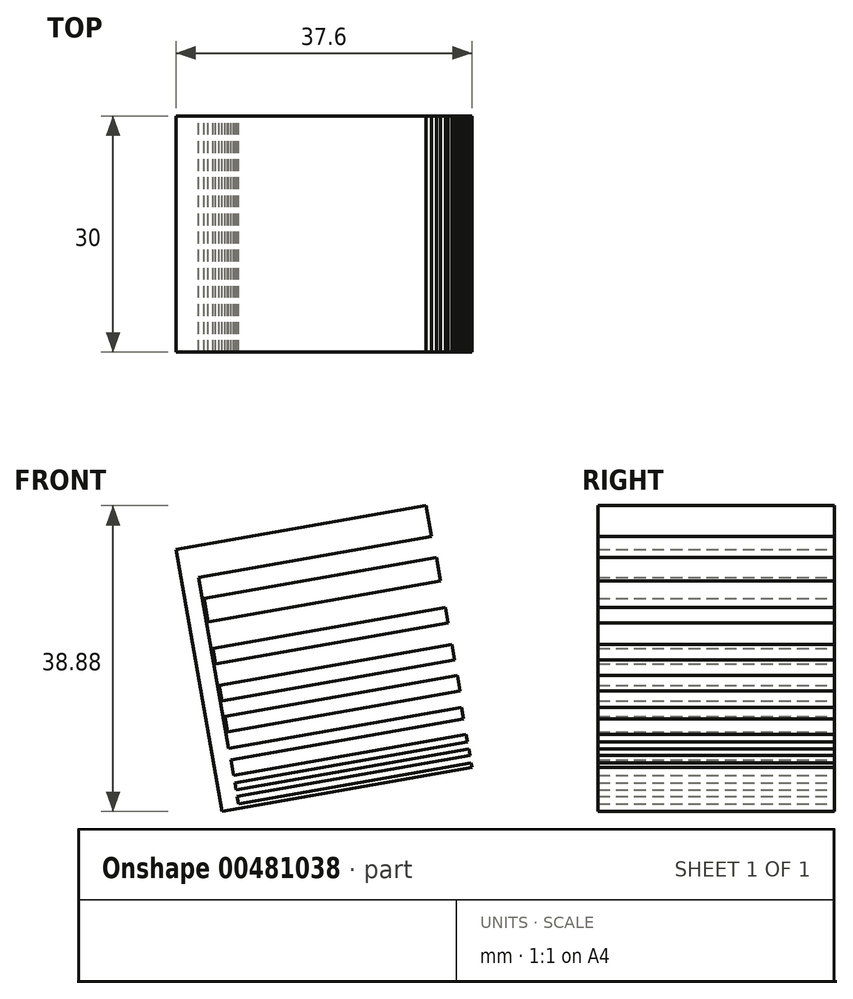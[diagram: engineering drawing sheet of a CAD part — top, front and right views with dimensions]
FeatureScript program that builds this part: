
annotation { "Feature Type Name" : "Feature", "Feature Type Description" : "" }
export const myFeature = defineFeature(function(context is Context, id is Id, definition is map)
    precondition{}
    {
        {
            var Q0;
            Q0=qCreatedBy(makeId("Front.planeOp"),FACE);
            var sketch = newSketch(context, id + "F0", { "sketchPlane" : qUnion([Q0])});
            skLineSegment(sketch, "E0.bottom", {"start": v(37.84, 14.06) * mm, "end": v(39.84, 14.06) * mm});
            skLineSegment(sketch, "E0.top", {"start": v(37.84, -15.94) * mm, "end": v(39.84, -15.94) * mm});
            skLineSegment(sketch, "E0.left", {"start": v(37.84, 14.06) * mm, "end": v(37.84, -15.94) * mm});
            skLineSegment(sketch, "E0.right", {"start": v(39.84, 14.06) * mm, "end": v(39.84, -15.94) * mm});
            skLineSegment(sketch, "E1.bottom", {"start": v(33.84, 14.06) * mm, "end": v(35.84, 14.06) * mm});
            skLineSegment(sketch, "E1.top", {"start": v(33.84, -15.94) * mm, "end": v(35.84, -15.94) * mm});
            skLineSegment(sketch, "E1.left", {"start": v(33.84, 14.06) * mm, "end": v(33.84, -15.94) * mm});
            skLineSegment(sketch, "E1.right", {"start": v(35.84, 14.06) * mm, "end": v(35.84, -15.94) * mm});
            skLineSegment(sketch, "E2.bottom", {"start": v(29.09, 14.06) * mm, "end": v(31.09, 14.06) * mm});
            skLineSegment(sketch, "E2.top", {"start": v(29.09, -15.94) * mm, "end": v(31.09, -15.94) * mm});
            skLineSegment(sketch, "E2.left", {"start": v(29.09, 14.06) * mm, "end": v(29.09, -15.94) * mm});
            skLineSegment(sketch, "E2.right", {"start": v(31.09, 14.06) * mm, "end": v(31.09, -15.94) * mm});
            skLineSegment(sketch, "E3.bottom", {"start": v(22.64, 14.06) * mm, "end": v(25.64, 14.06) * mm});
            skLineSegment(sketch, "E3.top", {"start": v(22.64, -15.94) * mm, "end": v(25.64, -15.94) * mm});
            skLineSegment(sketch, "E3.left", {"start": v(22.64, 14.06) * mm, "end": v(22.64, -15.94) * mm});
            skLineSegment(sketch, "E3.right", {"start": v(25.64, 14.06) * mm, "end": v(25.64, -15.94) * mm});
            skLineSegment(sketch, "E4.bottom", {"start": v(15.9, 13.86) * mm, "end": v(19.9, 13.86) * mm});
            skLineSegment(sketch, "E4.top", {"start": v(15.9, -16.14) * mm, "end": v(19.9, -16.14) * mm});
            skLineSegment(sketch, "E4.left", {"start": v(15.9, 13.86) * mm, "end": v(15.9, -16.14) * mm});
            skLineSegment(sketch, "E4.right", {"start": v(19.9, 13.86) * mm, "end": v(19.9, -16.14) * mm});
            skLineSegment(sketch, "E5.bottom", {"start": v(41.93, 13.86) * mm, "end": v(43.43, 13.86) * mm});
            skLineSegment(sketch, "E5.top", {"start": v(41.93, -16.14) * mm, "end": v(43.43, -16.14) * mm});
            skLineSegment(sketch, "E5.left", {"start": v(41.93, 13.86) * mm, "end": v(41.93, -16.14) * mm});
            skLineSegment(sketch, "E5.right", {"start": v(43.43, 13.86) * mm, "end": v(43.43, -16.14) * mm});
            skLineSegment(sketch, "E6.bottom", {"start": v(49.1, 13.86) * mm, "end": v(49.7, 13.86) * mm});
            skLineSegment(sketch, "E6.top", {"start": v(49.1, -16.14) * mm, "end": v(49.7, -16.14) * mm});
            skLineSegment(sketch, "E6.left", {"start": v(49.1, 13.86) * mm, "end": v(49.1, -16.14) * mm});
            skLineSegment(sketch, "E6.right", {"start": v(49.7, 13.86) * mm, "end": v(49.7, -16.14) * mm});
            skLineSegment(sketch, "E7.bottom", {"start": v(15.9, -16.14) * mm, "end": v(49.7, -16.14) * mm});
            skLineSegment(sketch, "E7.top", {"start": v(15.9, -18.36) * mm, "end": v(49.7, -18.36) * mm});
            skLineSegment(sketch, "E7.left", {"start": v(15.9, -16.14) * mm, "end": v(15.9, -18.36) * mm});
            skLineSegment(sketch, "E7.right", {"start": v(49.7, -16.14) * mm, "end": v(49.7, -18.36) * mm});
            skLineSegment(sketch, "E8.bottom", {"start": v(45.4, 13.86) * mm, "end": v(46.4, 13.86) * mm});
            skLineSegment(sketch, "E8.top", {"start": v(45.4, -16.14) * mm, "end": v(46.4, -16.14) * mm});
            skLineSegment(sketch, "E8.left", {"start": v(45.4, 13.86) * mm, "end": v(45.4, -16.14) * mm});
            skLineSegment(sketch, "E8.right", {"start": v(46.4, 13.86) * mm, "end": v(46.4, -16.14) * mm});
            skLineSegment(sketch, "E9.bottom", {"start": v(47.3, 13.86) * mm, "end": v(48.1, 13.86) * mm});
            skLineSegment(sketch, "E9.top", {"start": v(47.3, -16.14) * mm, "end": v(48.1, -16.14) * mm});
            skLineSegment(sketch, "E9.left", {"start": v(47.3, 13.86) * mm, "end": v(47.3, -16.14) * mm});
            skLineSegment(sketch, "E9.right", {"start": v(48.1, 13.86) * mm, "end": v(48.1, -16.14) * mm});
            skSolve(sketch);
        }
        {
            var Q0;
            Q0=makeQuery(id+"F0.imprint","IMPRINT",FACE,{"disambiguationData":[TD([[makeQuery(id+"F0.imprint","IMPRINT",EDGE,{"derivedFrom":sQuery(id+"F0.wireOp",EDGE,"E6.bottom")}),-1.0]])]});
            var Q1;
            Q1=makeQuery(id+"F0.imprint","IMPRINT",FACE,{"disambiguationData":[TD([[makeQuery(id+"F0.imprint","IMPRINT",EDGE,{"derivedFrom":sQuery(id+"F0.wireOp",EDGE,"E5.bottom")}),-1.0]])]});
            var Q2;
            Q2=makeQuery(id+"F0.imprint","IMPRINT",FACE,{"disambiguationData":[TD([[makeQuery(id+"F0.imprint","IMPRINT",EDGE,{"derivedFrom":sQuery(id+"F0.wireOp",EDGE,"E7.top")}),1.0]])]});
            var Q3;
            Q3=makeQuery(id+"F0.imprint","IMPRINT",FACE,{"disambiguationData":[TD([[makeQuery(id+"F0.imprint","IMPRINT",EDGE,{"derivedFrom":sQuery(id+"F0.wireOp",EDGE,"E8.bottom")}),-1.0]])]});
            var Q4;
            Q4=makeQuery(id+"F0.imprint","IMPRINT",FACE,{"disambiguationData":[TD([[makeQuery(id+"F0.imprint","IMPRINT",EDGE,{"derivedFrom":sQuery(id+"F0.wireOp",EDGE,"E9.bottom")}),-1.0]])]});
            var Q5;
            Q5=makeQuery(id+"F0.imprint","IMPRINT",FACE,{"disambiguationData":[TD([[makeQuery(id+"F0.imprint","IMPRINT",EDGE,{"derivedFrom":sQuery(id+"F0.wireOp",EDGE,"E3.bottom")}),-1.0]])]});
            var Q6;
            Q6=makeQuery(id+"F0.imprint","IMPRINT",FACE,{"disambiguationData":[TD([[makeQuery(id+"F0.imprint","IMPRINT",EDGE,{"derivedFrom":sQuery(id+"F0.wireOp",EDGE,"E4.bottom")}),-1.0]])]});
            var Q7;
            Q7=makeQuery(id+"F0.imprint","IMPRINT",FACE,{"disambiguationData":[TD([[makeQuery(id+"F0.imprint","IMPRINT",EDGE,{"derivedFrom":sQuery(id+"F0.wireOp",EDGE,"E1.bottom")}),-1.0]])]});
            var Q8;
            Q8=makeQuery(id+"F0.imprint","IMPRINT",FACE,{"disambiguationData":[TD([[makeQuery(id+"F0.imprint","IMPRINT",EDGE,{"derivedFrom":sQuery(id+"F0.wireOp",EDGE,"E0.bottom")}),-1.0]])]});
            var Q9;
            Q9=makeQuery(id+"F0.imprint","IMPRINT",FACE,{"disambiguationData":[TD([[makeQuery(id+"F0.imprint","IMPRINT",EDGE,{"derivedFrom":sQuery(id+"F0.wireOp",EDGE,"E2.bottom")}),-1.0]])]});
            extrude(context, id + "F1", {"entities" : qUnion([Q0, Q1, Q2, Q3, Q4, Q5, Q6, Q7, Q8, Q9]), "endBound" : BoundingType.SYMMETRIC, "depth" : 30 * mm});
        }
        {
            var Q0;
            Q0=makeQuery(id+"F1.opExtrude","SWEPT_BODY",BODY,{"disambiguationData":[OSD([sQuery(id+"F0.wireOp",EDGE,"E4.bottom"),sQuery(id+"F0.wireOp",EDGE,"E4.left"),sQuery(id+"F0.wireOp",EDGE,"E4.right"),sQuery(id+"F0.wireOp",EDGE,"E5.bottom"),sQuery(id+"F0.wireOp",EDGE,"E5.left"),sQuery(id+"F0.wireOp",EDGE,"E5.right"),sQuery(id+"F0.wireOp",EDGE,"E6.bottom"),sQuery(id+"F0.wireOp",EDGE,"E6.left"),sQuery(id+"F0.wireOp",EDGE,"E6.right"),sQuery(id+"F0.wireOp",EDGE,"E7.bottom"),sQuery(id+"F0.wireOp",EDGE,"E7.top"),sQuery(id+"F0.wireOp",EDGE,"E7.left"),sQuery(id+"F0.wireOp",EDGE,"E7.right"),sQuery(id+"F0.wireOp",EDGE,"E8.bottom"),sQuery(id+"F0.wireOp",EDGE,"E8.left"),sQuery(id+"F0.wireOp",EDGE,"E8.right"),sQuery(id+"F0.wireOp",EDGE,"E9.bottom"),sQuery(id+"F0.wireOp",EDGE,"E9.left"),sQuery(id+"F0.wireOp",EDGE,"E9.right")])]});
            var Q1;
            Q1=makeQuery(id+"F1.opExtrude","SWEPT_BODY",BODY,{"disambiguationData":[OSD([sQuery(id+"F0.wireOp",EDGE,"E3.bottom"),sQuery(id+"F0.wireOp",EDGE,"E3.top"),sQuery(id+"F0.wireOp",EDGE,"E3.left"),sQuery(id+"F0.wireOp",EDGE,"E3.right")])]});
            var Q2;
            Q2=makeQuery(id+"F1.opExtrude","SWEPT_BODY",BODY,{"disambiguationData":[OSD([sQuery(id+"F0.wireOp",EDGE,"E2.bottom"),sQuery(id+"F0.wireOp",EDGE,"E2.top"),sQuery(id+"F0.wireOp",EDGE,"E2.left"),sQuery(id+"F0.wireOp",EDGE,"E2.right")])]});
            var Q3;
            Q3=makeQuery(id+"F1.opExtrude","SWEPT_BODY",BODY,{"disambiguationData":[OSD([sQuery(id+"F0.wireOp",EDGE,"E1.bottom"),sQuery(id+"F0.wireOp",EDGE,"E1.top"),sQuery(id+"F0.wireOp",EDGE,"E1.left"),sQuery(id+"F0.wireOp",EDGE,"E1.right")])]});
            var Q4;
            Q4=makeQuery(id+"F1.opExtrude","SWEPT_BODY",BODY,{"disambiguationData":[OSD([sQuery(id+"F0.wireOp",EDGE,"E0.bottom"),sQuery(id+"F0.wireOp",EDGE,"E0.top"),sQuery(id+"F0.wireOp",EDGE,"E0.left"),sQuery(id+"F0.wireOp",EDGE,"E0.right")])]});
            var Q5;
            Q5=makeQuery(id+"F1.opExtrude","SWEPT_EDGE",EDGE,{"disambiguationData":[OSD([sQuery(id+"F0.wireOp",EDGE,"E7.top"),sQuery(id+"F0.wireOp",EDGE,"E7.right")])]});
            transform(context, id + "F2", {"entities" : qUnion([Q0, Q1, Q2, Q3, Q4]), "transformType" : TransformType.ROTATION, "transformAxis" : qUnion([Q5]), "angle" : 80 * degree, "makeCopy" : false});
        }
    });
